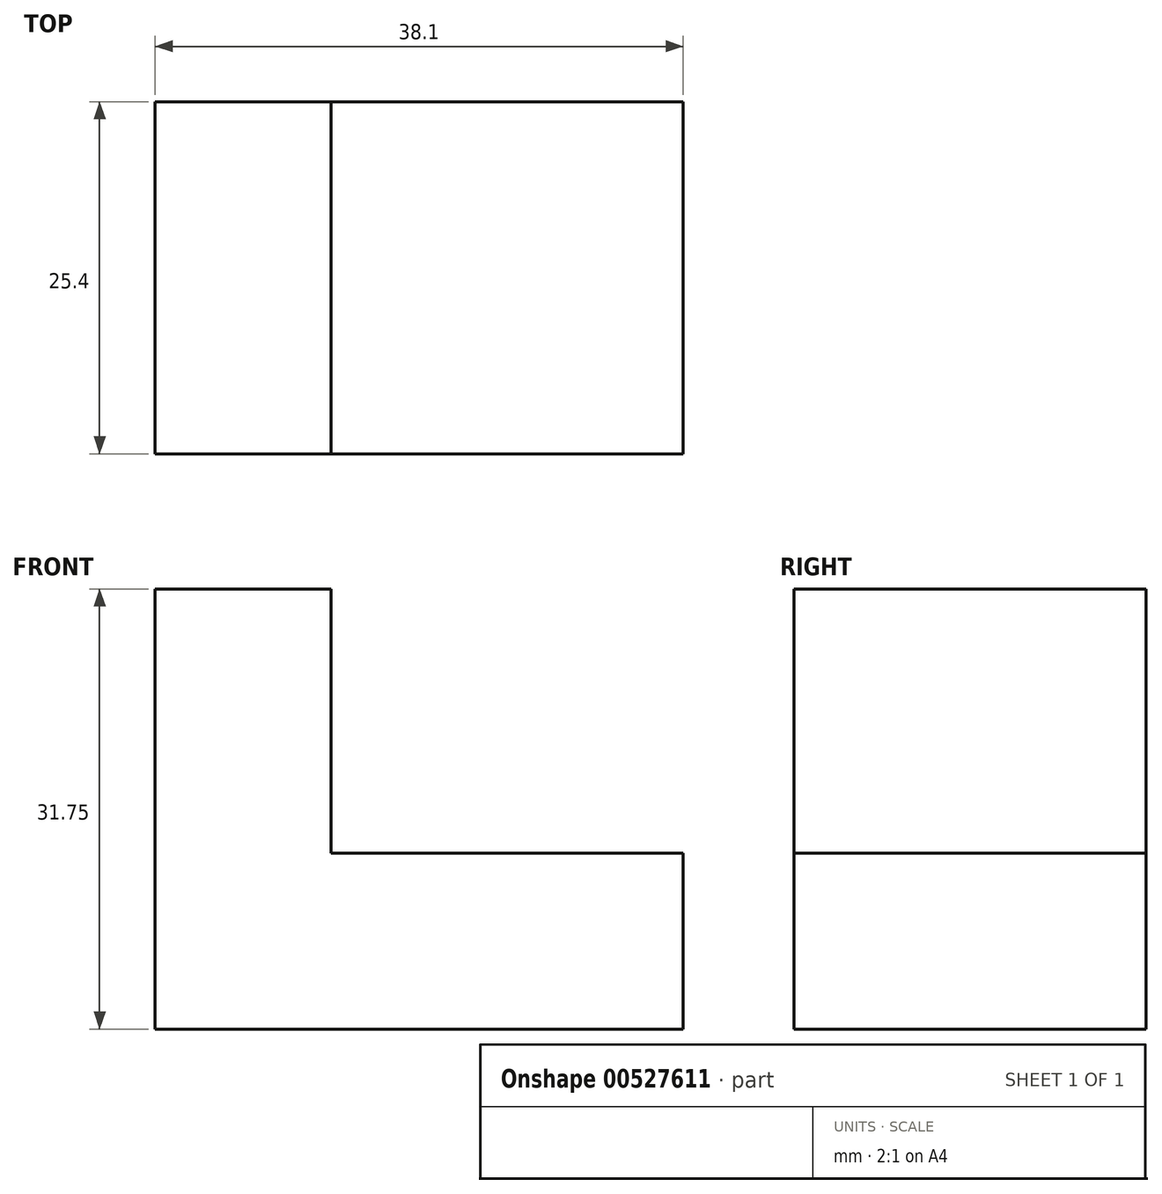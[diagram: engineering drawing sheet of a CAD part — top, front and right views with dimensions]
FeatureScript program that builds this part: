
annotation { "Feature Type Name" : "Feature", "Feature Type Description" : "" }
export const myFeature = defineFeature(function(context is Context, id is Id, definition is map)
    precondition{}
    {
        {
            var Q0;
            Q0=qCreatedBy(makeId("Front.planeOp"),FACE);
            var sketch = newSketch(context, id + "F0", { "sketchPlane" : qUnion([Q0])});
            skLineSegment(sketch, "E0.bottom", {"start": v(0, 0) * mm, "end": v(38.1, 0) * mm});
            skLineSegment(sketch, "E0.top", {"start": v(12.7, 12.7) * mm, "end": v(38.1, 12.7) * mm});
            skLineSegment(sketch, "E0.left", {"start": v(0, 0) * mm, "end": v(0, 12.7) * mm});
            skLineSegment(sketch, "E0.right", {"start": v(38.1, 0) * mm, "end": v(38.1, 12.7) * mm});
            skLineSegment(sketch, "E1.bottom", {"start": v(0, 0) * mm, "end": v(12.7, 0) * mm});
            skLineSegment(sketch, "E1.top", {"start": v(0, 31.75) * mm, "end": v(12.7, 31.75) * mm});
            skLineSegment(sketch, "E1.left", {"start": v(0, 0) * mm, "end": v(0, 31.75) * mm});
            skLineSegment(sketch, "E1.right", {"start": v(12.7, 12.7) * mm, "end": v(12.7, 31.75) * mm});
            skSolve(sketch);
        }
        {
            var Q0;
            Q0=makeQuery(id+"F0.imprint","IMPRINT",FACE,{"disambiguationData":[TD([[makeQuery(id+"F0.imprint","IMPRINT",EDGE,{"derivedFrom":sQuery(id+"F0.wireOp",EDGE,"E0.bottom")}),1.0]])]});
            var sketch = newSketch(context, id + "F1", { "sketchPlane" : qUnion([Q0])});
            skSolve(sketch);
        }
        {
            var Q0;
            Q0 = qSketchRegion(id + "F1", true);
            var Q1;
            Q1=makeQuery(id+"F0.imprint","IMPRINT",FACE,{"disambiguationData":[TD([[makeQuery(id+"F0.imprint","IMPRINT",EDGE,{"derivedFrom":sQuery(id+"F0.wireOp",EDGE,"E0.bottom")}),1.0]])]});
            extrude(context, id + "F2", {"entities" : qUnion([Q0, Q1]), "depth" : 25.4 * mm, "offsetDistance" : 25.4 * mm});
        }
    });
